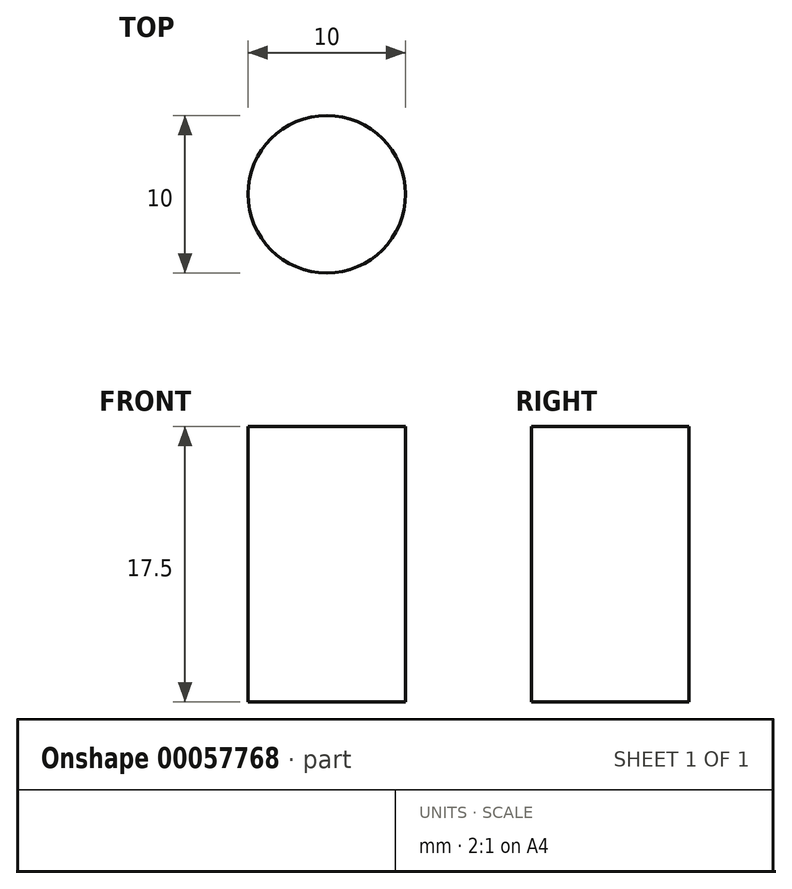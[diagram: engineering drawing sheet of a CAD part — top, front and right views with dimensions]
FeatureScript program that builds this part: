
annotation { "Feature Type Name" : "Feature", "Feature Type Description" : "" }
export const myFeature = defineFeature(function(context is Context, id is Id, definition is map)
    precondition{}
    {
        {
            var Q0;
            Q0=qCreatedBy(makeId("Top.planeOp"),FACE);
            var sketch = newSketch(context, id + "F0", { "sketchPlane" : qUnion([Q0])});
            skCircle(sketch, "E0", {"center": v(0, 0) * mm, "radius": 5 * mm});
            skSolve(sketch);
        }
        {
            var Q0;
            Q0=makeQuery(id+"F0.imprint","IMPRINT",FACE,{"disambiguationData":[TD([[makeQuery(id+"F0.imprint","IMPRINT",EDGE,{"derivedFrom":sQuery(id+"F0.wireOp",EDGE,"E0")}),1.0]])]});
            extrude(context, id + "F1", {"entities" : qUnion([Q0]), "depth" : 17.5 * mm});
        }
    });
